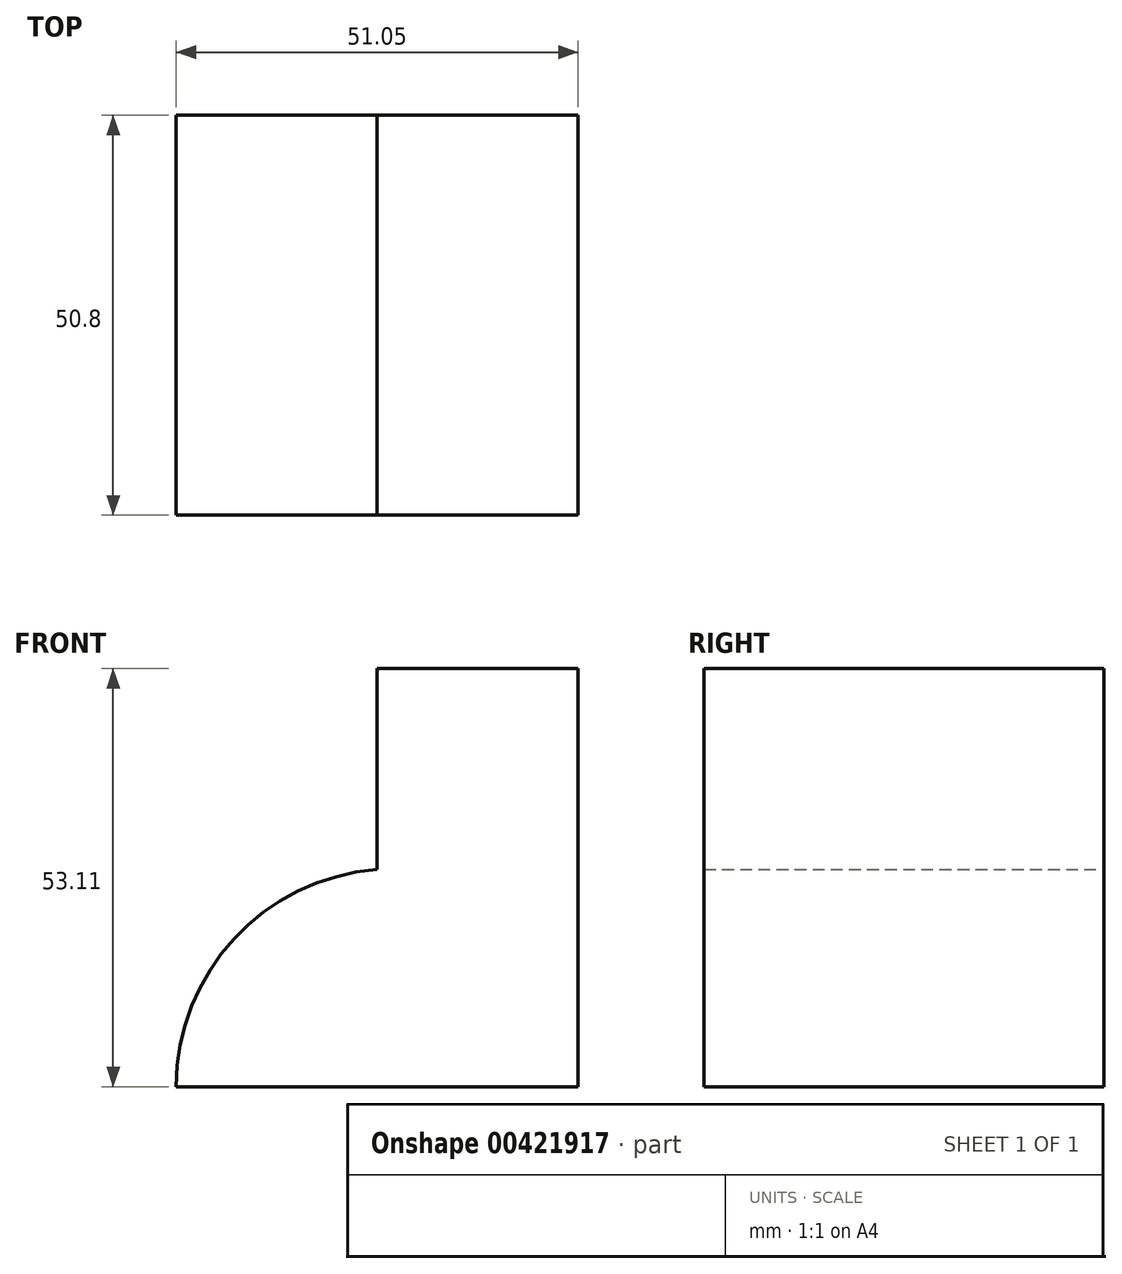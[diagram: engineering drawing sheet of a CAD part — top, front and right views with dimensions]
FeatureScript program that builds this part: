
annotation { "Feature Type Name" : "Feature", "Feature Type Description" : "" }
export const myFeature = defineFeature(function(context is Context, id is Id, definition is map)
    precondition{}
    {
        {
            var Q0;
            Q0=qCreatedBy(makeId("Front.planeOp"),FACE);
            var sketch = newSketch(context, id + "F0", { "sketchPlane" : qUnion([Q0])});
            skLineSegment(sketch, "E0", {"start": v(0, 0) * mm, "end": v(0, 53.11) * mm});
            skLineSegment(sketch, "E1", {"start": v(0, 0) * mm, "end": v(-51.05, 0) * mm});
            skLineSegment(sketch, "E2", {"start": v(0, 53.11) * mm, "end": v(-25.53, 53.11) * mm});
            skLineSegment(sketch, "E3", {"start": v(-25.53, 53.11) * mm, "end": v(-25.53, 27.58) * mm});
            skArc(sketch, "E4", {"start": v(-25.53, 27.58) * mm, "mid": v(-43.7, 18.8) * mm, "end": v(-51.05, 0) * mm});
            skPoint(sketch, "E5.start.orphan", {"position": v(-51.05, 27.58) * mm});
            skSolve(sketch);
        }
        {
            var Q0;
            Q0=makeQuery(id+"F0.imprint","IMPRINT",FACE,{"disambiguationData":[TD([[makeQuery(id+"F0.imprint","IMPRINT",EDGE,{"derivedFrom":sQuery(id+"F0.wireOp",EDGE,"E0")}),1.0]])]});
            extrude(context, id + "F1", {"entities" : qUnion([Q0]), "depth" : 50.8 * mm});
        }
    });
